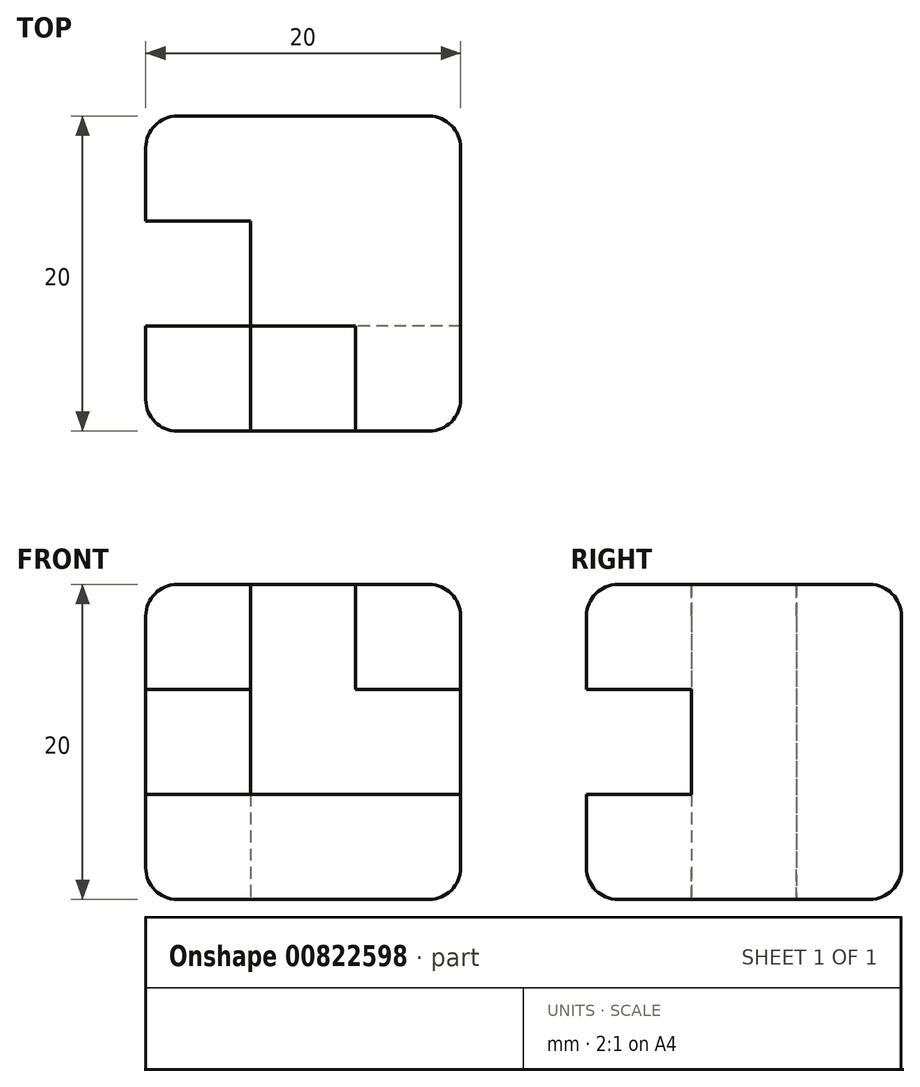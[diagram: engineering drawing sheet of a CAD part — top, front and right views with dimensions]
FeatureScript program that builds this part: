
annotation { "Feature Type Name" : "Feature", "Feature Type Description" : "" }
export const myFeature = defineFeature(function(context is Context, id is Id, definition is map)
    precondition{}
    {
        {
            assignVariable(context, id + "F0", {"name" : "Side", "anyValue" : 20});
        }
        {
            var Q0;
            Q0=qCreatedBy(makeId("Top.planeOp"),FACE);
            var sketch = newSketch(context, id + "F1", { "sketchPlane" : qUnion([Q0])});
            skLineSegment(sketch, "E0.bottom", {"start": v(-10.22, 10.44) * mm, "end": v(9.78, 10.44) * mm});
            skLineSegment(sketch, "E0.top", {"start": v(-10.22, -9.56) * mm, "end": v(9.78, -9.56) * mm});
            skLineSegment(sketch, "E0.left", {"start": v(-10.22, 10.44) * mm, "end": v(-10.22, -9.56) * mm});
            skLineSegment(sketch, "E0.right", {"start": v(9.78, 10.44) * mm, "end": v(9.78, -9.56) * mm});
            skSolve(sketch);
        }
        {
            var Q0;
            Q0 = qSketchRegion(id + "F1", true);
            extrude(context, id + "F2", {"entities" : qUnion([Q0]), "depth" : (getVariable(context, 'Side')) * mm, "offsetDistance" : 25 * mm});
        }
        {
            var Q0;
            Q0=makeQuery(id+"F2.opExtrude","SWEPT_FACE",FACE,{"disambiguationData":[OSD([sQuery(id+"F1.wireOp",EDGE,"E0.left")])]});
            var sketch = newSketch(context, id + "F3", { "sketchPlane" : qUnion([Q0])});
            skLineSegment(sketch, "E1.bottom", {"start": v(-3.77, 20) * mm, "end": v(2.9, 20) * mm});
            skLineSegment(sketch, "E1.top", {"start": v(-3.77, 0) * mm, "end": v(2.9, 0) * mm});
            skLineSegment(sketch, "E1.left", {"start": v(-3.77, 20) * mm, "end": v(-3.77, 0) * mm});
            skLineSegment(sketch, "E1.right", {"start": v(2.9, 20) * mm, "end": v(2.9, 0) * mm});
            skSolve(sketch);
        }
        {
            var Q0;
            Q0 = qSketchRegion(id + "F3", true);
            extrude(context, id + "F4", {"entities" : qUnion([Q0]), "operationType" : NewBodyOperationType.REMOVE, "oppositeDirection" : true, "depth" : (getVariable(context, 'Side') / 3) * mm, "offsetDistance" : 25 * mm});
        }
        {
            var Q0;
            {var subQ1=sQuery(id+"F1.wireOp",EDGE,"E0.left");var subQ2=sQuery(id+"F1.wireOp",EDGE,"E0.top");Q0=makeQuery(id+"F4.boolean.opBoolean","SPLIT",FACE,{"disambiguationData":[TD([makeQuery(id+"F2.opExtrude","SWEPT_FACE",FACE,{"disambiguationData":[OSD([subQ2])]})])],"derivedFrom":makeQuery(id+"F2.opExtrude","SWEPT_FACE",FACE,{"disambiguationData":[OSD([subQ1])]})});}
            var sketch = newSketch(context, id + "F5", { "sketchPlane" : qUnion([Q0])});
            skLineSegment(sketch, "E2.bottom", {"start": v(2.9, 13.33) * mm, "end": v(9.56, 13.33) * mm});
            skLineSegment(sketch, "E2.top", {"start": v(2.9, 6.67) * mm, "end": v(9.56, 6.67) * mm});
            skLineSegment(sketch, "E2.left", {"start": v(2.9, 13.33) * mm, "end": v(2.9, 6.67) * mm});
            skLineSegment(sketch, "E2.right", {"start": v(9.56, 13.33) * mm, "end": v(9.56, 6.67) * mm});
            skSolve(sketch);
        }
        {
            var Q0;
            Q0 = qSketchRegion(id + "F5", true);
            extrude(context, id + "F6", {"entities" : qUnion([Q0]), "operationType" : NewBodyOperationType.REMOVE, "oppositeDirection" : true, "depth" : (getVariable(context, 'Side') / 3 * 2) * mm, "offsetDistance" : 25 * mm});
        }
        {
            var Q0;
            Q0=makeQuery(id+"F2.opExtrude","SWEPT_FACE",FACE,{"disambiguationData":[OSD([sQuery(id+"F1.wireOp",EDGE,"E0.top")])]});
            var sketch = newSketch(context, id + "F7", { "sketchPlane" : qUnion([Q0])});
            skLineSegment(sketch, "E3.bottom", {"start": v(-3.56, 20) * mm, "end": v(3.11, 20) * mm});
            skLineSegment(sketch, "E3.top", {"start": v(-3.56, 13.33) * mm, "end": v(3.11, 13.33) * mm});
            skLineSegment(sketch, "E3.left", {"start": v(-3.56, 20) * mm, "end": v(-3.56, 13.33) * mm});
            skLineSegment(sketch, "E3.right", {"start": v(3.11, 20) * mm, "end": v(3.11, 13.33) * mm});
            skLineSegment(sketch, "E4.bottom", {"start": v(3.11, 13.33) * mm, "end": v(9.78, 13.33) * mm});
            skLineSegment(sketch, "E4.top", {"start": v(3.11, 6.67) * mm, "end": v(9.78, 6.67) * mm});
            skLineSegment(sketch, "E4.left", {"start": v(3.11, 13.33) * mm, "end": v(3.11, 6.67) * mm});
            skLineSegment(sketch, "E4.right", {"start": v(9.78, 13.33) * mm, "end": v(9.78, 6.67) * mm});
            skSolve(sketch);
        }
        {
            var Q0;
            Q0 = qSketchRegion(id + "F7", true);
            extrude(context, id + "F8", {"entities" : qUnion([Q0]), "operationType" : NewBodyOperationType.REMOVE, "oppositeDirection" : true, "depth" : (getVariable(context, 'Side') / 3) * mm, "offsetDistance" : 25 * mm});
        }
        {
            var Q0;
            {var subQ0=sQuery(id+"F1.wireOp",EDGE,"E0.bottom");var subQ1=sQuery(id+"F1.wireOp",EDGE,"E0.left");Q0=makeQuery(id+"F4.boolean.opBoolean","SPLIT",EDGE,{"disambiguationData":[TD([makeQuery(id+"F2.opExtrude","SWEPT_FACE",FACE,{"disambiguationData":[OSD([subQ0])]})])],"derivedFrom":makeQuery(id+"F2.opExtrude","CAP_EDGE",EDGE,{"disambiguationData":[OSD([subQ1])],"isStart":false})});}
            var Q1;
            Q1=makeQuery(id+"F2.opExtrude","SWEPT_EDGE",EDGE,{"disambiguationData":[OSD([sQuery(id+"F1.wireOp",EDGE,"E0.bottom"),sQuery(id+"F1.wireOp",EDGE,"E0.left")])]});
            var Q2;
            {var subQ0=sQuery(id+"F1.wireOp",EDGE,"E0.bottom");var subQ1=sQuery(id+"F1.wireOp",EDGE,"E0.left");Q2=makeQuery(id+"F4.boolean.opBoolean","SPLIT",EDGE,{"disambiguationData":[TD([makeQuery(id+"F2.opExtrude","SWEPT_FACE",FACE,{"disambiguationData":[OSD([subQ0])]})])],"derivedFrom":makeQuery(id+"F2.opExtrude","CAP_EDGE",EDGE,{"disambiguationData":[OSD([subQ1])],"isStart":true})});}
            var Q3;
            {var subQ0=sQuery(id+"F1.wireOp",EDGE,"E0.left");var subQ1=sQuery(id+"F1.wireOp",EDGE,"E0.top");Q3=makeQuery(id+"F4.boolean.opBoolean","SPLIT",EDGE,{"disambiguationData":[TD([makeQuery(id+"F2.opExtrude","SWEPT_FACE",FACE,{"disambiguationData":[OSD([subQ1])]})])],"derivedFrom":makeQuery(id+"F2.opExtrude","CAP_EDGE",EDGE,{"disambiguationData":[OSD([subQ0])],"isStart":true})});}
            var Q4;
            Q4=makeQuery(id+"F2.opExtrude","CAP_EDGE",EDGE,{"disambiguationData":[OSD([sQuery(id+"F1.wireOp",EDGE,"E0.top")])],"isStart":true});
            var Q5;
            {var subQ0=sQuery(id+"F1.wireOp",EDGE,"E0.left");var subQ1=sQuery(id+"F1.wireOp",EDGE,"E0.top");Q5=makeQuery(id+"F6.boolean.opBoolean","SPLIT",EDGE,{"disambiguationData":[TD([makeQuery(id+"F6.opExtrude","SWEPT_FACE",FACE,{"disambiguationData":[OSD([sQuery(id+"F5.wireOp",EDGE,"E2.bottom")])]})])],"derivedFrom":makeQuery(id+"F2.opExtrude","SWEPT_EDGE",EDGE,{"disambiguationData":[OSD([subQ1,subQ0])]})});}
            var Q6;
            {var subQ0=sQuery(id+"F1.wireOp",EDGE,"E0.left");var subQ1=sQuery(id+"F1.wireOp",EDGE,"E0.top");Q6=makeQuery(id+"F4.boolean.opBoolean","SPLIT",EDGE,{"disambiguationData":[TD([makeQuery(id+"F2.opExtrude","SWEPT_FACE",FACE,{"disambiguationData":[OSD([subQ1])]})])],"derivedFrom":makeQuery(id+"F2.opExtrude","CAP_EDGE",EDGE,{"disambiguationData":[OSD([subQ0])],"isStart":false})});}
            var Q7;
            {var subQ0=sQuery(id+"F1.wireOp",EDGE,"E0.left");var subQ1=sQuery(id+"F1.wireOp",EDGE,"E0.top");Q7=makeQuery(id+"F8.boolean.opBoolean","SPLIT",EDGE,{"disambiguationData":[TD([makeQuery(id+"F2.opExtrude","SWEPT_FACE",FACE,{"disambiguationData":[OSD([subQ0])]})])],"derivedFrom":makeQuery(id+"F2.opExtrude","CAP_EDGE",EDGE,{"disambiguationData":[OSD([subQ1])],"isStart":false})});}
            var Q8;
            {var subQ0=sQuery(id+"F1.wireOp",EDGE,"E0.right");var subQ1=sQuery(id+"F1.wireOp",EDGE,"E0.top");Q8=makeQuery(id+"F8.boolean.opBoolean","SPLIT",EDGE,{"disambiguationData":[TD([makeQuery(id+"F6.boolean.opBoolean","COPY",FACE,{"derivedFrom":makeQuery(id+"F6.opExtrude","SWEPT_FACE",FACE,{"disambiguationData":[OSD([sQuery(id+"F5.wireOp",EDGE,"E2.bottom")])]})})])],"derivedFrom":makeQuery(id+"F2.opExtrude","SWEPT_EDGE",EDGE,{"disambiguationData":[OSD([subQ1,subQ0])]})});}
            var Q9;
            {var subQ0=sQuery(id+"F1.wireOp",EDGE,"E0.right");var subQ1=sQuery(id+"F1.wireOp",EDGE,"E0.top");Q9=makeQuery(id+"F8.boolean.opBoolean","SPLIT",EDGE,{"disambiguationData":[TD([makeQuery(id+"F2.opExtrude","SWEPT_FACE",FACE,{"disambiguationData":[OSD([subQ0])]})])],"derivedFrom":makeQuery(id+"F2.opExtrude","CAP_EDGE",EDGE,{"disambiguationData":[OSD([subQ1])],"isStart":false})});}
            var Q10;
            Q10=makeQuery(id+"F2.opExtrude","CAP_EDGE",EDGE,{"disambiguationData":[OSD([sQuery(id+"F1.wireOp",EDGE,"E0.right")])],"isStart":false});
            var Q11;
            Q11=makeQuery(id+"F2.opExtrude","CAP_EDGE",EDGE,{"disambiguationData":[OSD([sQuery(id+"F1.wireOp",EDGE,"E0.right")])],"isStart":true});
            var Q12;
            Q12=makeQuery(id+"F2.opExtrude","SWEPT_EDGE",EDGE,{"disambiguationData":[OSD([sQuery(id+"F1.wireOp",EDGE,"E0.bottom"),sQuery(id+"F1.wireOp",EDGE,"E0.right")])]});
            var Q13;
            Q13=makeQuery(id+"F2.opExtrude","CAP_EDGE",EDGE,{"disambiguationData":[OSD([sQuery(id+"F1.wireOp",EDGE,"E0.bottom")])],"isStart":true});
            var Q14;
            Q14=makeQuery(id+"F2.opExtrude","CAP_EDGE",EDGE,{"disambiguationData":[OSD([sQuery(id+"F1.wireOp",EDGE,"E0.bottom")])],"isStart":false});
            var Q15;
            {var subQ0=sQuery(id+"F1.wireOp",EDGE,"E0.left");var subQ1=sQuery(id+"F1.wireOp",EDGE,"E0.top");Q15=makeQuery(id+"F6.boolean.opBoolean","SPLIT",EDGE,{"disambiguationData":[TD([makeQuery(id+"F6.opExtrude","SWEPT_FACE",FACE,{"disambiguationData":[OSD([sQuery(id+"F5.wireOp",EDGE,"E2.top")])]})])],"derivedFrom":makeQuery(id+"F2.opExtrude","SWEPT_EDGE",EDGE,{"disambiguationData":[OSD([subQ1,subQ0])]})});}
            var Q16;
            {var subQ0=sQuery(id+"F1.wireOp",EDGE,"E0.right");var subQ1=sQuery(id+"F1.wireOp",EDGE,"E0.top");Q16=makeQuery(id+"F8.boolean.opBoolean","SPLIT",EDGE,{"disambiguationData":[TD([makeQuery(id+"F6.boolean.opBoolean","COPY",FACE,{"derivedFrom":makeQuery(id+"F6.opExtrude","SWEPT_FACE",FACE,{"disambiguationData":[OSD([sQuery(id+"F5.wireOp",EDGE,"E2.top")])]})})])],"derivedFrom":makeQuery(id+"F2.opExtrude","SWEPT_EDGE",EDGE,{"disambiguationData":[OSD([subQ1,subQ0])]})});}
            fillet(context, id + "F9", {"entities" : qUnion([Q0, Q1, Q2, Q3, Q4, Q5, Q6, Q7, Q8, Q9, Q10, Q11, Q12, Q13, Q14, Q15, Q16]), "radius" : (getVariable(context, 'Side') / 10) * mm, "tangentPropagation" : true, "allowEdgeOverflow" : false});
        }
    });
